# Revit family: 2058956
name_source: partatom
category: Lighting Fixtures
revit_build: Autodesk Revit 2018 (Build: 20170223_1515(x64)
units: mm (PartAtom-declared; Revit-internal decimal feet)

## family parameters
Cut with Voids When Loaded = No
Host = Face
Light Source = Yes
OmniClass Number = 23.80.70.11.17
OmniClass Title = Specialized Lighting by Location or Use
Part Type = Normal
Room Calculation Point = No
Round Connector Dimension = Use Diameter
Shared = No

## types (1)
- 2058956 MYRIAD DECO IP65 SP 3K PHD BK CBEZ
    Accessory Diameter = 90 mm  [stored 0.295276 ft]
    Accessory Inner Diameter 1 = 88 mm  [stored 0.288714 ft]
    Accessory Inner Diameter 2 = 68 mm  [stored 0.223097 ft]
    Accessory Material = Aluminum_Sylvania_Myriad_White
    Apparent Load = 10 VA
    Assembly Code = D5020200
    AssetType = Fixed
    Body Material = Aluminum_Sylvania_Myriad_Gray
    Body Radius = 36.5 mm  [stored 0.119751 ft]
    Color Filter = 16777215
    Cost = 0 $
    Cutout Diameter = 75 mm
    Default Elevation = 0 mm  [stored 0 ft]
    Description = Supplied complete with electronic control gear Compact Fluorescent low energy downlight Emergency version passes through the cut out Ideal for low level orientation lighting New range of Architectural accessories each providing a different lit dimension New completely flush plaster up accessory ring for clean ceiling lines and smooth finish Order lamp separately
    Diffuser Diameter = 75 mm
    Diffuser Material = Glass_Sylvania_Myriad_Clear_4000K
    Dimming Lamp Color Temperature Shift = <None>
    DocumentationLiterature = http://www.sylvania-lighting.com
    DurationUnit = hours
    ElectricShockClassification = 111
    Emit Shape Visible in Rendering = No
    Emit from Circle Diameter = 68 mm  [stored 0.223097 ft]
    ExpectedLife = 50000
    Height = 72 mm  [stored 0.23622 ft]
    IfcExportAs = Class II
    IfcExportType = IfcLightFixtureType
    ImpactProtectionIndex = IfcLightFixtureType
    IngressProtection = IfcLightFixtureType
    InputNominalFrequency = 3000
    InputVoltage = 0
    Keynote_2 = 16500
    LampColourRenderingIndex = 16500
    LampColourTemperature = LED
    LampMacAdamStep = 90
    LampNominalLuminous = 3000 K
    LightOutputRatio = LED
    LuminaireType = 0
    Manufacturer = Feilo Sylvania
    ManufacturerName = 111 lm/W
    Material = Feilo Sylvania
    Model = MYRIAD DECO IP65 SPOT 3000K PHDM BLACK CBEZ
    ModelNumber = 2058956
    ModelReference = MYRIAD DECO IP65 SPOT 3000K PHDM BLACK CBEZ
    Name = MYRIAD DECO IP65 SPOT 3000K PHDM BLACK CBEZ
    NominalHeight = 72 mm  [stored 0.23622 ft]
    NominalLength = 76 mm  [stored 0.249344 ft]
    NominalWidth = 0 mm  [stored 0 ft]
    Photometric Web File = 2058956.ies
    PowerConsumption = Lighting
    PowerFactor = 0
    Recessed Depth = 72 mm  [stored 0.23622 ft]
    Reflector Material = Aluminum_Sylvania_Myriad_Bright
    Reflector Radius = 35 mm
    Tilt Angle = -90°
    Type Image = <None>
    TypeName = MYRIAD DECO IP65 SPOT 3000K PHDM BLACK CBEZ
    URL = 0
    Voltage = 230 V
    WarrantyDescription = http://www.sylvania-lighting.com

note: [stored X ft] marks values corroborated as IEEE doubles in the binary element streams (Revit-internal decimal feet)

## geometry (parser evidence)
native form markers: Sweep x1
no freeform markers — native parametric forms only
